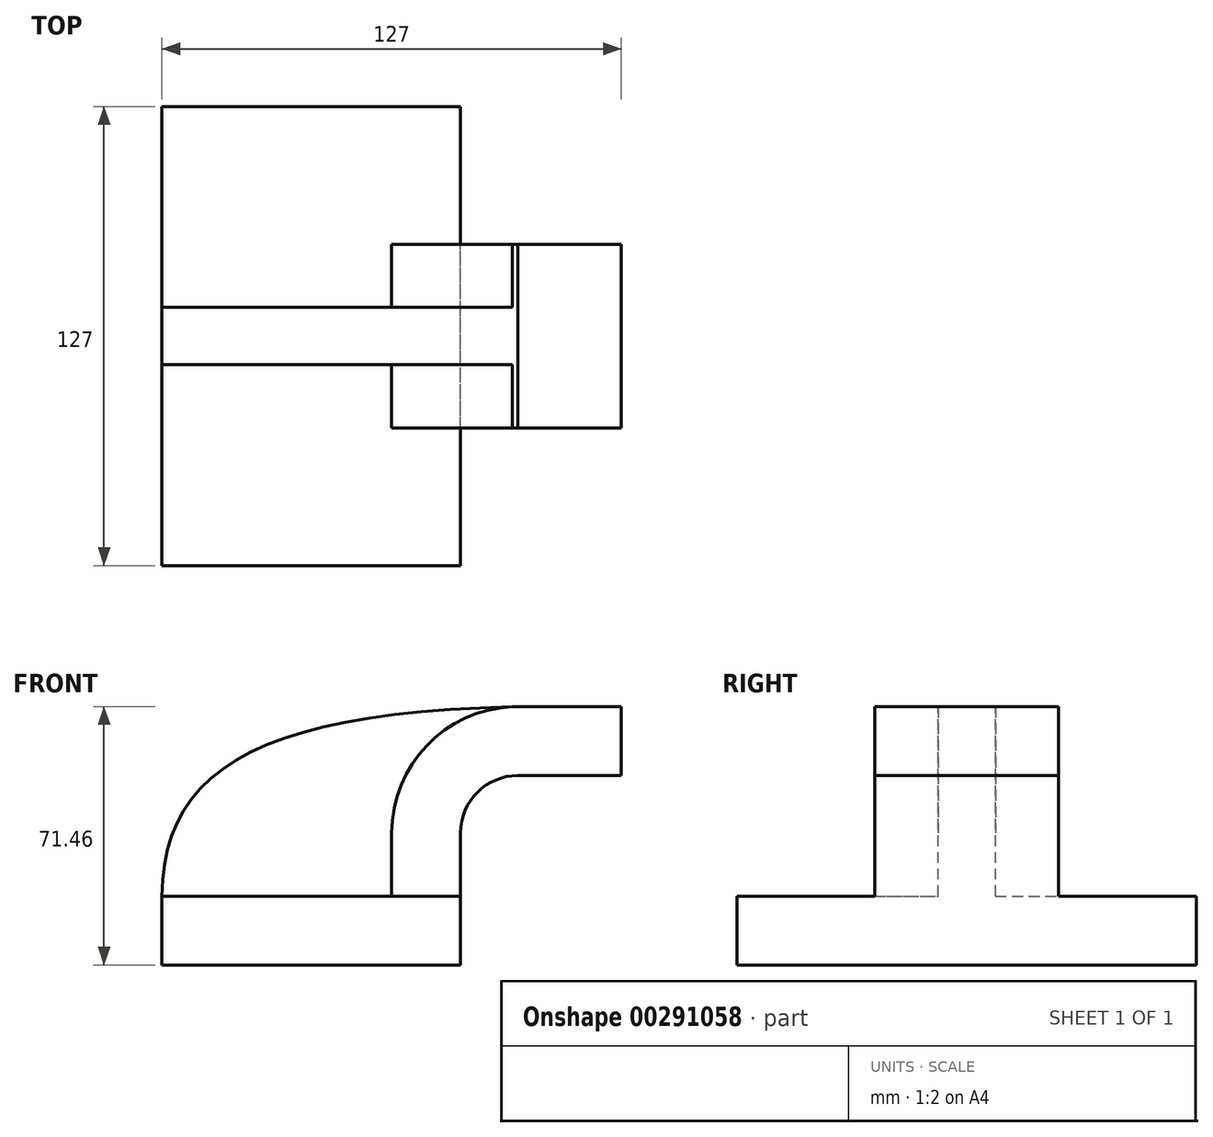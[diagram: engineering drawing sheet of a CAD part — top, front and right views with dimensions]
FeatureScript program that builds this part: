
annotation { "Feature Type Name" : "Feature", "Feature Type Description" : "" }
export const myFeature = defineFeature(function(context is Context, id is Id, definition is map)
    precondition{}
    {
        {
            var Q0;
            Q0=qCreatedBy(makeId("Front.planeOp"),FACE);
            var sketch = newSketch(context, id + "F0", { "sketchPlane" : qUnion([Q0])});
            skLineSegment(sketch, "E0.bottom", {"start": v(41.28, 9.53) * mm, "end": v(-41.28, 9.53) * mm});
            skLineSegment(sketch, "E0.top", {"start": v(41.28, -9.53) * mm, "end": v(-41.28, -9.53) * mm});
            skLineSegment(sketch, "E0.left", {"start": v(41.28, 9.52) * mm, "end": v(41.28, -9.53) * mm});
            skLineSegment(sketch, "E0.right", {"start": v(-41.28, 9.53) * mm, "end": v(-41.28, -9.53) * mm});
            skPoint(sketch, "E0.middle", {"position": v(0, 0) * mm});
            skLineSegment(sketch, "E1.bottom", {"start": v(111.13, 34.93) * mm, "end": v(60.33, 34.93) * mm});
            skLineSegment(sketch, "E1.top", {"start": v(111.13, 66.67) * mm, "end": v(60.33, 66.67) * mm});
            skLineSegment(sketch, "E1.left", {"start": v(111.13, 34.93) * mm, "end": v(111.13, 66.68) * mm});
            skLineSegment(sketch, "E1.right", {"start": v(60.33, 34.93) * mm, "end": v(60.33, 66.68) * mm});
            skPoint(sketch, "E1.middle", {"position": v(85.73, 50.8) * mm});
            skLineSegment(sketch, "E2", {"start": v(41.28, 9.53) * mm, "end": v(41.28, 27) * mm});
            skArc(sketch, "E3", {"start": v(41.28, 27) * mm, "mid": v(45.92, 38.23) * mm, "end": v(57.15, 42.88) * mm});
            skLineSegment(sketch, "E4", {"start": v(57.15, 42.88) * mm, "end": v(85.72, 42.88) * mm});
            skLineSegment(sketch, "E5.0", {"start": v(57.15, 61.93) * mm, "end": v(85.72, 61.93) * mm});
            skArc(sketch, "E5.1", {"start": v(22.23, 27) * mm, "mid": v(32.45, 51.7) * mm, "end": v(57.15, 61.93) * mm});
            skLineSegment(sketch, "E5.2", {"start": v(22.23, 9.53) * mm, "end": v(22.23, 27) * mm});
            skLineSegment(sketch, "E6", {"start": v(85.73, 34.93) * mm, "end": v(85.73, 66.67) * mm});
            skFitSpline(sketch, "E7", {"points": [v(-41.28, 9.53) * mm, v(57.15, 61.93) * mm], "startDerivative": vector(0.83, 105.88) * mm, "endDerivative": vector(212.33, 4.4) * mm});
            skSolve(sketch);
        }
        {
            var Q0;
            Q0=makeQuery(id+"F0.imprint","IMPRINT",FACE,{"disambiguationData":[TD([[makeQuery(id+"F0.imprint","IMPRINT",EDGE,{"derivedFrom":sQuery(id+"F0.wireOp",EDGE,"E0.top")}),-1.0]])]});
            extrude(context, id + "F1", {"entities" : qUnion([Q0]), "endBound" : BoundingType.SYMMETRIC, "depth" : 127 * mm});
        }
        {
            var Q0;
            {var subQ1=sQuery(id+"F0.wireOp",EDGE,"E2");Q0=makeQuery(id+"F0.imprint","IMPRINT",FACE,{"disambiguationData":[TD([[makeQuery(id+"F0.imprint","IMPRINT",EDGE,{"derivedFrom":subQ1}),1.0]])]});}
            var Q1;
            {var subQ0=sQuery(id+"F0.wireOp",EDGE,"E4");var subQ1=sQuery(id+"F0.wireOp",EDGE,"E1.right");var subQ2=makeQuery(id+"F0.imprint","INTERSECT",VERTEX,{"derivedFrom":[subQ1,subQ0]});Q1=makeQuery(id+"F0.imprint","IMPRINT",FACE,{"disambiguationData":[TD([[makeQuery(id+"F0.imprint","IMPRINT",EDGE,{"disambiguationData":[TD([[subQ2,-1.0]])],"derivedFrom":subQ1}),-1.0]])]});}
            extrude(context, id + "F2", {"entities" : qUnion([Q0, Q1]), "operationType" : NewBodyOperationType.ADD, "endBound" : BoundingType.SYMMETRIC, "depth" : 50.8 * mm});
        }
        {
            var Q0;
            {var subQ3=sQuery(id+"F0.wireOp",EDGE,"E5.2");Q0=makeQuery(id+"F0.imprint","IMPRINT",FACE,{"disambiguationData":[TD([[makeQuery(id+"F0.imprint","IMPRINT",EDGE,{"derivedFrom":subQ3}),1.0]])]});}
            extrude(context, id + "F3", {"entities" : qUnion([Q0]), "operationType" : NewBodyOperationType.ADD, "endBound" : BoundingType.SYMMETRIC, "depth" : 15.88 * mm});
        }
    });
